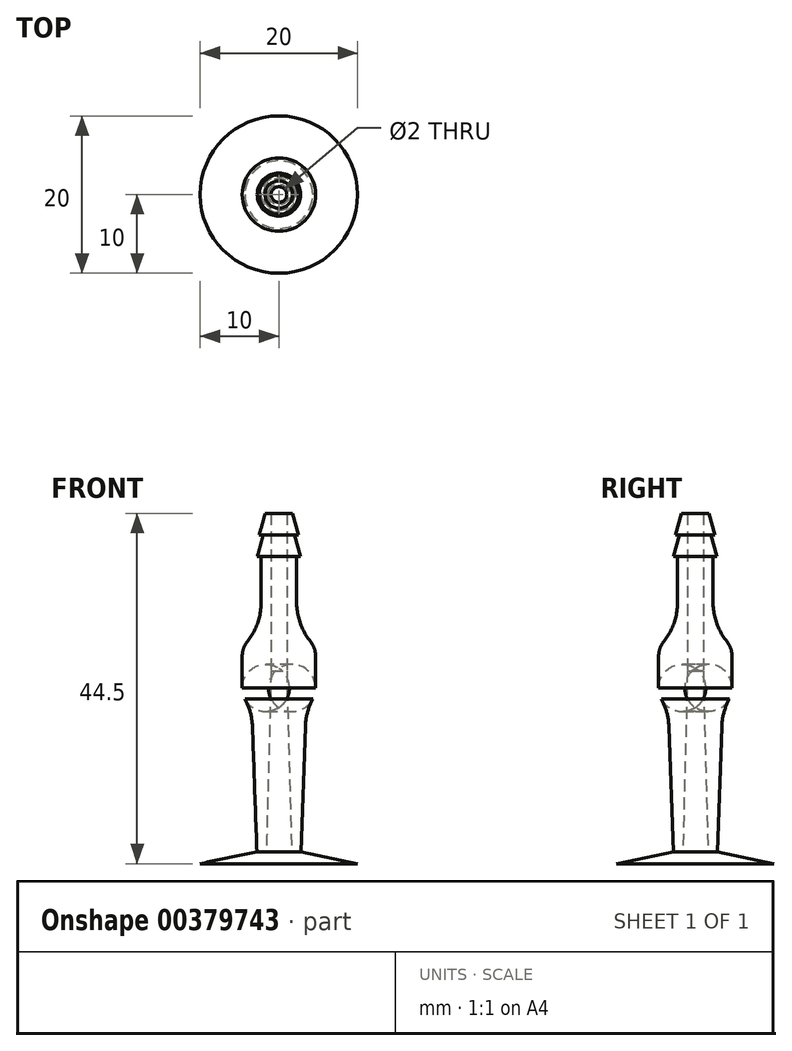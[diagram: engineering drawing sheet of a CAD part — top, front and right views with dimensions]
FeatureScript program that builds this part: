
annotation { "Feature Type Name" : "Feature", "Feature Type Description" : "" }
export const myFeature = defineFeature(function(context is Context, id is Id, definition is map)
    precondition{}
    {
        {
            var Q0;
            Q0=qCreatedBy(makeId("Front.planeOp"),FACE);
            var sketch = newSketch(context, id + "F0", { "sketchPlane" : qUnion([Q0])});
            skLineSegment(sketch, "E0", {"start": v(0, 0) * mm, "end": v(0, 20) * mm, "construction": true});
            skLineSegment(sketch, "E1", {"start": v(0, 20) * mm, "end": v(-1.75, 20) * mm});
            skLineSegment(sketch, "E2", {"start": v(-1.75, 20) * mm, "end": v(-2.5, 17.25) * mm});
            skLineSegment(sketch, "E3", {"start": v(-2.5, 17.25) * mm, "end": v(-2, 17.25) * mm});
            skLineSegment(sketch, "E4", {"start": v(-2, 17.25) * mm, "end": v(-2.75, 14.5) * mm});
            skLineSegment(sketch, "E5", {"start": v(-2.75, 14.5) * mm, "end": v(-2.25, 14.5) * mm});
            skLineSegment(sketch, "E6", {"start": v(-2.25, 14.5) * mm, "end": v(-2.25, 3) * mm});
            skLineSegment(sketch, "E7", {"start": v(-1, 20) * mm, "end": v(-1, 0) * mm});
            skLineSegment(sketch, "E8", {"start": v(-2.25, 3) * mm, "end": v(-4.66, 3) * mm});
            skLineSegment(sketch, "E9", {"start": v(-4.66, 3) * mm, "end": v(-4.66, -3) * mm});
            skLineSegment(sketch, "E10", {"start": v(-4.66, -3) * mm, "end": v(-3.5, -3) * mm});
            skLineSegment(sketch, "E11", {"start": v(-3.5, -3) * mm, "end": v(-2.8, -23) * mm});
            skLineSegment(sketch, "E12", {"start": v(-2.8, -23) * mm, "end": v(-1.6, -23) * mm});
            skPoint(sketch, "E13.orphan", {"position": v(-2.25, 3) * mm});
            skLineSegment(sketch, "E14", {"start": v(-1, 0) * mm, "end": v(-1.6, -23) * mm});
            skLineSegment(sketch, "E15", {"start": v(-2.8, -23) * mm, "end": v(-10, -24.5) * mm});
            skLineSegment(sketch, "E16", {"start": v(-10, -24.5) * mm, "end": v(0, -24.5) * mm});
            skLineSegment(sketch, "E17", {"start": v(0, -24.5) * mm, "end": v(0, -23) * mm});
            skLineSegment(sketch, "E18", {"start": v(0, -23) * mm, "end": v(-1.6, -23) * mm});
            skSolve(sketch);
        }
        {
            var Q0;
            {var subQ1=sQuery(id+"F0.wireOp",EDGE,"E2");Q0=makeQuery(id+"F0.imprint","IMPRINT",FACE,{"disambiguationData":[TD([[makeQuery(id+"F0.imprint","IMPRINT",EDGE,{"derivedFrom":subQ1}),1.0]])]});}
            var Q1;
            Q1=makeQuery(id+"F0.imprint","IMPRINT",FACE,{"disambiguationData":[TD([[makeQuery(id+"F0.imprint","IMPRINT",EDGE,{"derivedFrom":sQuery(id+"F0.wireOp",EDGE,"E12")}),-1.0]])]});
            var Q2;
            Q2=sQuery(id+"F0.wireOp",EDGE,"E0");
            revolve(context, id + "F1", {"entities" : qUnion([Q0, Q1]), "axis" : qUnion([Q2]), "revolveType" : RevolveType.FULL});
        }
        {
            var Q0;
            Q0=makeQuery(id+"F1.opRevolve","SWEPT_EDGE",EDGE,{"disambiguationData":[OSD([sQuery(id+"F0.wireOp",EDGE,"E6"),sQuery(id+"F0.wireOp",EDGE,"E8")])]});
            var Q1;
            Q1=makeQuery(id+"F1.opRevolve","SWEPT_EDGE",EDGE,{"disambiguationData":[OSD([sQuery(id+"F0.wireOp",EDGE,"E10"),sQuery(id+"F0.wireOp",EDGE,"E11")])]});
            fillet(context, id + "F2", {"entities" : qUnion([Q0, Q1]), "radius" : 8 * mm, "tangentPropagation" : true, "allowEdgeOverflow" : false});
        }
        {
            var Q0;
            Q0=makeQuery(id+"F2.opFillet","BLEND_EDGE",EDGE,{"blendedFrom":[makeQuery(id+"F1.opRevolve","SWEPT_EDGE",EDGE,{"disambiguationData":[OSD([sQuery(id+"F0.wireOp",EDGE,"E6"),sQuery(id+"F0.wireOp",EDGE,"E8")])]}),makeQuery(id+"F1.opRevolve","SWEPT_FACE",FACE,{"disambiguationData":[OSD([sQuery(id+"F0.wireOp",EDGE,"E9")])]})],"blendedInto":[makeQuery(id+"F1.opRevolve","SWEPT_FACE",FACE,{"disambiguationData":[OSD([sQuery(id+"F0.wireOp",EDGE,"E9")])]})]});
            var Q1;
            Q1=makeQuery(id+"F2.opFillet","BLEND_EDGE",EDGE,{"blendedFrom":[makeQuery(id+"F1.opRevolve","SWEPT_EDGE",EDGE,{"disambiguationData":[OSD([sQuery(id+"F0.wireOp",EDGE,"E10"),sQuery(id+"F0.wireOp",EDGE,"E11")])]}),makeQuery(id+"F1.opRevolve","SWEPT_FACE",FACE,{"disambiguationData":[OSD([sQuery(id+"F0.wireOp",EDGE,"E9")])]})],"blendedInto":[makeQuery(id+"F1.opRevolve","SWEPT_FACE",FACE,{"disambiguationData":[OSD([sQuery(id+"F0.wireOp",EDGE,"E9")])]})]});
            fillet(context, id + "F3", {"entities" : qUnion([Q0, Q1]), "radius" : 3 * mm, "tangentPropagation" : true, "allowEdgeOverflow" : false});
        }
    });
